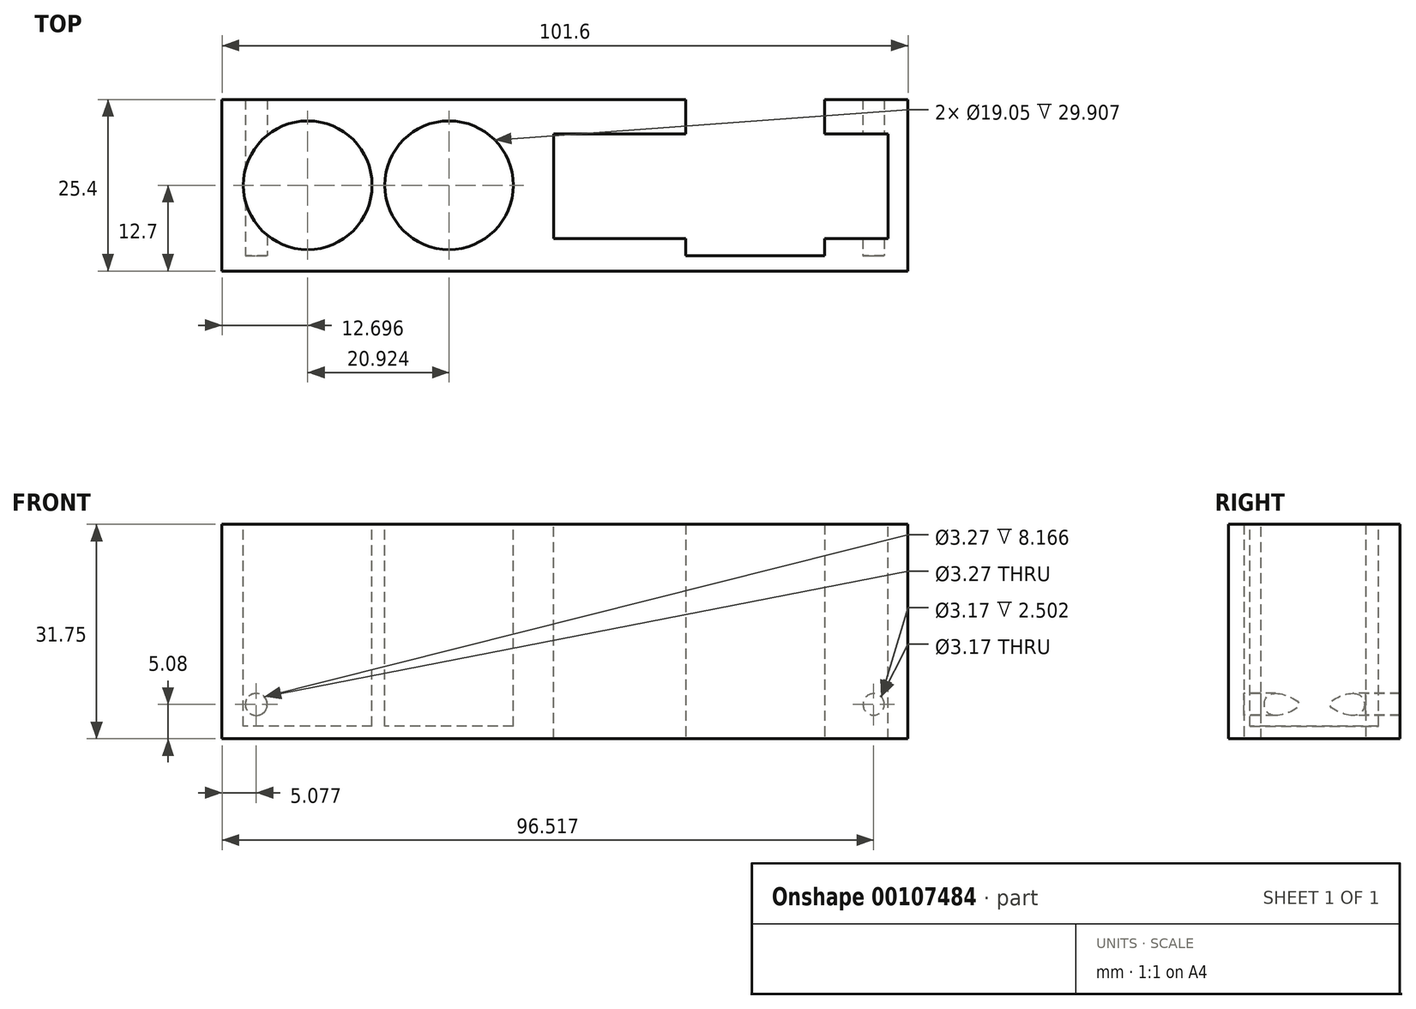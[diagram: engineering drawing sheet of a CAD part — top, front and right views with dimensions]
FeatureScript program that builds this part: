
annotation { "Feature Type Name" : "Feature", "Feature Type Description" : "" }
export const myFeature = defineFeature(function(context is Context, id is Id, definition is map)
    precondition{}
    {
        {
            var Q0;
            Q0=qCreatedBy(makeId("Front.planeOp"),FACE);
            var sketch = newSketch(context, id + "F0", { "sketchPlane" : qUnion([Q0])});
            skLineSegment(sketch, "E0.bottom", {"start": v(-33.62, -10.06) * mm, "end": v(67.98, -10.06) * mm});
            skLineSegment(sketch, "E0.top", {"start": v(-33.62, -41.81) * mm, "end": v(67.98, -41.81) * mm});
            skLineSegment(sketch, "E0.left", {"start": v(-33.62, -10.06) * mm, "end": v(-33.62, -41.81) * mm});
            skLineSegment(sketch, "E0.right", {"start": v(67.98, -10.06) * mm, "end": v(67.98, -41.81) * mm});
            skSolve(sketch);
        }
        {
            var Q0;
            Q0 = qSketchRegion(id + "F0", true);
            extrude(context, id + "F1", {"entities" : qUnion([Q0]), "depth" : 25.4 * mm});
        }
        {
            var Q0;
            Q0=makeQuery(id+"F1.opExtrude","SWEPT_FACE",FACE,{"disambiguationData":[OSD([sQuery(id+"F0.wireOp",EDGE,"E0.bottom")])]});
            var sketch = newSketch(context, id + "F2", { "sketchPlane" : qUnion([Q0])});
            skCircle(sketch, "E1", {"center": v(-20.92, -12.7) * mm, "radius": 9.53 * mm});
            skPoint(sketch, "E1.centerSnap0", {"position": v(-33.62, -12.7) * mm});
            skCircle(sketch, "E2", {"center": v(0, -12.7) * mm, "radius": 9.53 * mm});
            skLineSegment(sketch, "E3.bottom", {"start": v(15.5, -20.61) * mm, "end": v(65.03, -20.61) * mm});
            skLineSegment(sketch, "E3.top", {"start": v(15.5, -5.1) * mm, "end": v(65.03, -5.1) * mm});
            skLineSegment(sketch, "E3.left", {"start": v(15.5, -20.61) * mm, "end": v(15.5, -5.1) * mm});
            skLineSegment(sketch, "E3.right", {"start": v(65.03, -20.61) * mm, "end": v(65.03, -5.1) * mm});
            skLineSegment(sketch, "E4", {"start": v(40.26, -5.1) * mm, "end": v(40.26, 0) * mm});
            skLineSegment(sketch, "E5", {"start": v(-9.51, -13.23) * mm, "end": v(-11.41, -13.23) * mm, "construction": true});
            skSolve(sketch);
        }
        {
            var Q0;
            Q0 = qSketchRegion(id + "F2", true);
            extrude(context, id + "F3", {"entities" : qUnion([Q0]), "operationType" : NewBodyOperationType.REMOVE, "oppositeDirection" : true, "depth" : 29.9 * mm});
        }
        {
            var Q0;
            Q0=makeQuery(id+"F1.opExtrude","CAP_FACE",FACE,{"disambiguationData":[OSD([sQuery(id+"F0.wireOp",EDGE,"E0.bottom"),sQuery(id+"F0.wireOp",EDGE,"E0.top"),sQuery(id+"F0.wireOp",EDGE,"E0.left"),sQuery(id+"F0.wireOp",EDGE,"E0.right")])],"isStart":false});
            var sketch = newSketch(context, id + "F4", { "sketchPlane" : qUnion([Q0])});
            skCircle(sketch, "E6", {"center": v(-28.54, -36.73) * mm, "radius": 1.63 * mm});
            skCircle(sketch, "E7", {"center": v(62.9, -36.73) * mm, "radius": 1.59 * mm});
            skLineSegment(sketch, "E8", {"start": v(-28.54, -36.73) * mm, "end": v(-28.54, -41.81) * mm, "construction": true});
            skLineSegment(sketch, "E9", {"start": v(-28.54, -36.73) * mm, "end": v(-33.62, -36.73) * mm, "construction": true});
            skLineSegment(sketch, "E10", {"start": v(62.9, -36.73) * mm, "end": v(67.98, -36.73) * mm, "construction": true});
            skLineSegment(sketch, "E11", {"start": v(62.9, -41.81) * mm, "end": v(62.9, -36.73) * mm, "construction": true});
            skLineSegment(sketch, "E12", {"start": v(45.44, -10.06) * mm, "end": v(45.44, -48.16) * mm, "construction": true});
            skLineSegment(sketch, "E13.bottom", {"start": v(35.04, -10.06) * mm, "end": v(55.65, -10.06) * mm});
            skLineSegment(sketch, "E13.top", {"start": v(35.04, -48.22) * mm, "end": v(55.65, -48.22) * mm});
            skLineSegment(sketch, "E13.left", {"start": v(35.04, -10.06) * mm, "end": v(35.04, -48.22) * mm});
            skLineSegment(sketch, "E13.right", {"start": v(55.65, -10.06) * mm, "end": v(55.65, -48.22) * mm});
            skSolve(sketch);
        }
        {
            var Q0;
            Q0 = qSketchRegion(id + "F4", true);
            extrude(context, id + "F5", {"entities" : qUnion([Q0]), "operationType" : NewBodyOperationType.REMOVE, "oppositeDirection" : true, "depth" : 25.4 * mm});
        }
        {
            var Q0;
            Q0=makeQuery(id+"F4.imprint","IMPRINT",FACE,{"disambiguationData":[TD([[makeQuery(id+"F4.imprint","IMPRINT",EDGE,{"derivedFrom":sQuery(id+"F4.wireOp",EDGE,"E6")}),1.0]])]});
            var Q1;
            Q1=makeQuery(id+"F4.imprint","IMPRINT",FACE,{"disambiguationData":[TD([[makeQuery(id+"F4.imprint","IMPRINT",EDGE,{"derivedFrom":sQuery(id+"F4.wireOp",EDGE,"E7")}),1.0]])]});
            var Q2;
            {var subQ0=sQuery(id+"F4.wireOp",EDGE,"E13.bottom");Q2=makeQuery(id+"F4.imprint","IMPRINT",FACE,{"disambiguationData":[TD([[makeQuery(id+"F4.imprint","IMPRINT",EDGE,{"derivedFrom":subQ0}),-1.0]])]});}
            var Q3;
            {var subQ0=sQuery(id+"F4.wireOp",EDGE,"E13.top");Q3=makeQuery(id+"F4.imprint","IMPRINT",FACE,{"disambiguationData":[TD([[makeQuery(id+"F4.imprint","IMPRINT",EDGE,{"derivedFrom":subQ0}),1.0]])]});}
            extrude(context, id + "F6", {"entities" : qUnion([Q0, Q1, Q2, Q3]), "operationType" : NewBodyOperationType.ADD, "oppositeDirection" : true, "depth" : 2.3 * mm});
        }
        {
            var Q0;
            Q0=makeQuery(id+"F2.imprint","IMPRINT",FACE,{"disambiguationData":[TD([[makeQuery(id+"F2.imprint","IMPRINT",EDGE,{"derivedFrom":sQuery(id+"F2.wireOp",EDGE,"E3.bottom")}),1.0]])]});
            extrude(context, id + "F7", {"entities" : qUnion([Q0]), "operationType" : NewBodyOperationType.REMOVE, "oppositeDirection" : true, "depth" : 76.2 * mm});
        }
        {
            var Q0;
            Q0=makeQuery(id+"F6.opExtrude","SWEPT_FACE",FACE,{"disambiguationData":[OSD([sQuery(id+"F4.wireOp",EDGE,"E13.top")])]});
            var Q1;
            {var subQ0=sQuery(id+"F0.wireOp",EDGE,"E0.right");var subQ2=sQuery(id+"F0.wireOp",EDGE,"E0.top");Q1=makeQuery(id+"F5.boolean.opBoolean","SPLIT",FACE,{"disambiguationData":[TD([makeQuery(id+"F1.opExtrude","SWEPT_FACE",FACE,{"disambiguationData":[OSD([subQ0])]})])],"derivedFrom":makeQuery(id+"F1.opExtrude","SWEPT_FACE",FACE,{"disambiguationData":[OSD([subQ2])]})});}
            extrude(context, id + "F8", {"entities" : qUnion([Q0]), "operationType" : NewBodyOperationType.REMOVE, "endBound" : BoundingType.UP_TO_SURFACE, "oppositeDirection" : true, "endBoundEntityFace" : qUnion([Q1]), "depth" : 25.4 * mm});
        }
    });
